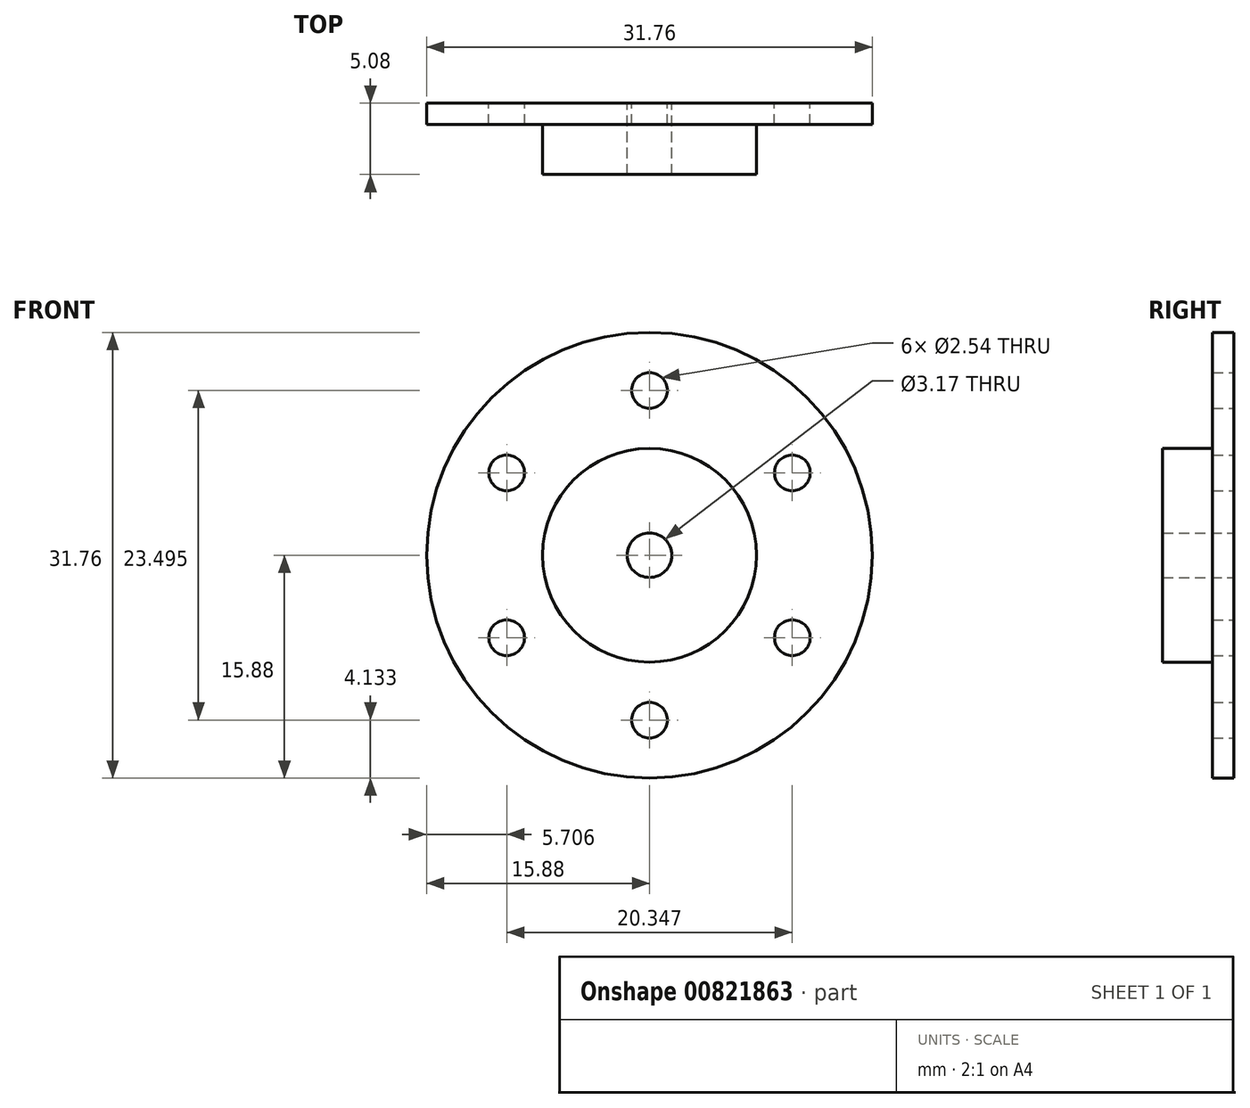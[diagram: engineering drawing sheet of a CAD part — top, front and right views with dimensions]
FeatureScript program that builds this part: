
annotation { "Feature Type Name" : "Feature", "Feature Type Description" : "" }
export const myFeature = defineFeature(function(context is Context, id is Id, definition is map)
    precondition{}
    {
        {
            var Q0;
            Q0=qCreatedBy(makeId("Front.planeOp"),FACE);
            var sketch = newSketch(context, id + "F0", { "sketchPlane" : qUnion([Q0])});
            skCircle(sketch, "E0", {"center": v(0, 0) * mm, "radius": 15.88 * mm});
            skCircle(sketch, "E1", {"center": v(0, 0) * mm, "radius": 7.62 * mm});
            skCircle(sketch, "E2", {"center": v(0, 0) * mm, "radius": 1.59 * mm});
            skCircle(sketch, "E3", {"center": v(0, 11.75) * mm, "radius": 1.27 * mm});
            skCircle(sketch, "E4.1.0", {"center": v(-10.17, 5.87) * mm, "radius": 1.27 * mm});
            skCircle(sketch, "E4.2.0", {"center": v(-10.17, -5.87) * mm, "radius": 1.27 * mm});
            skCircle(sketch, "E4.3.0", {"center": v(0, -11.75) * mm, "radius": 1.27 * mm});
            skCircle(sketch, "E4.4.0", {"center": v(10.17, -5.87) * mm, "radius": 1.27 * mm});
            skCircle(sketch, "E4.5.0", {"center": v(10.17, 5.87) * mm, "radius": 1.27 * mm});
            skSolve(sketch);
        }
        {
            var Q0;
            Q0=makeQuery(id+"F0.imprint","IMPRINT",FACE,{"disambiguationData":[TD([[makeQuery(id+"F0.imprint","IMPRINT",EDGE,{"derivedFrom":sQuery(id+"F0.wireOp",EDGE,"E0")}),1.0]])]});
            extrude(context, id + "F1", {"entities" : qUnion([Q0]), "depth" : 1.52 * mm, "offsetDistance" : 25.4 * mm});
        }
        {
            var Q0;
            Q0=makeQuery(id+"F0.imprint","IMPRINT",FACE,{"disambiguationData":[TD([[makeQuery(id+"F0.imprint","IMPRINT",EDGE,{"derivedFrom":sQuery(id+"F0.wireOp",EDGE,"E1")}),1.0]])]});
            extrude(context, id + "F2", {"entities" : qUnion([Q0]), "operationType" : NewBodyOperationType.ADD, "depth" : 5.08 * mm, "offsetDistance" : 25.4 * mm});
        }
    });
